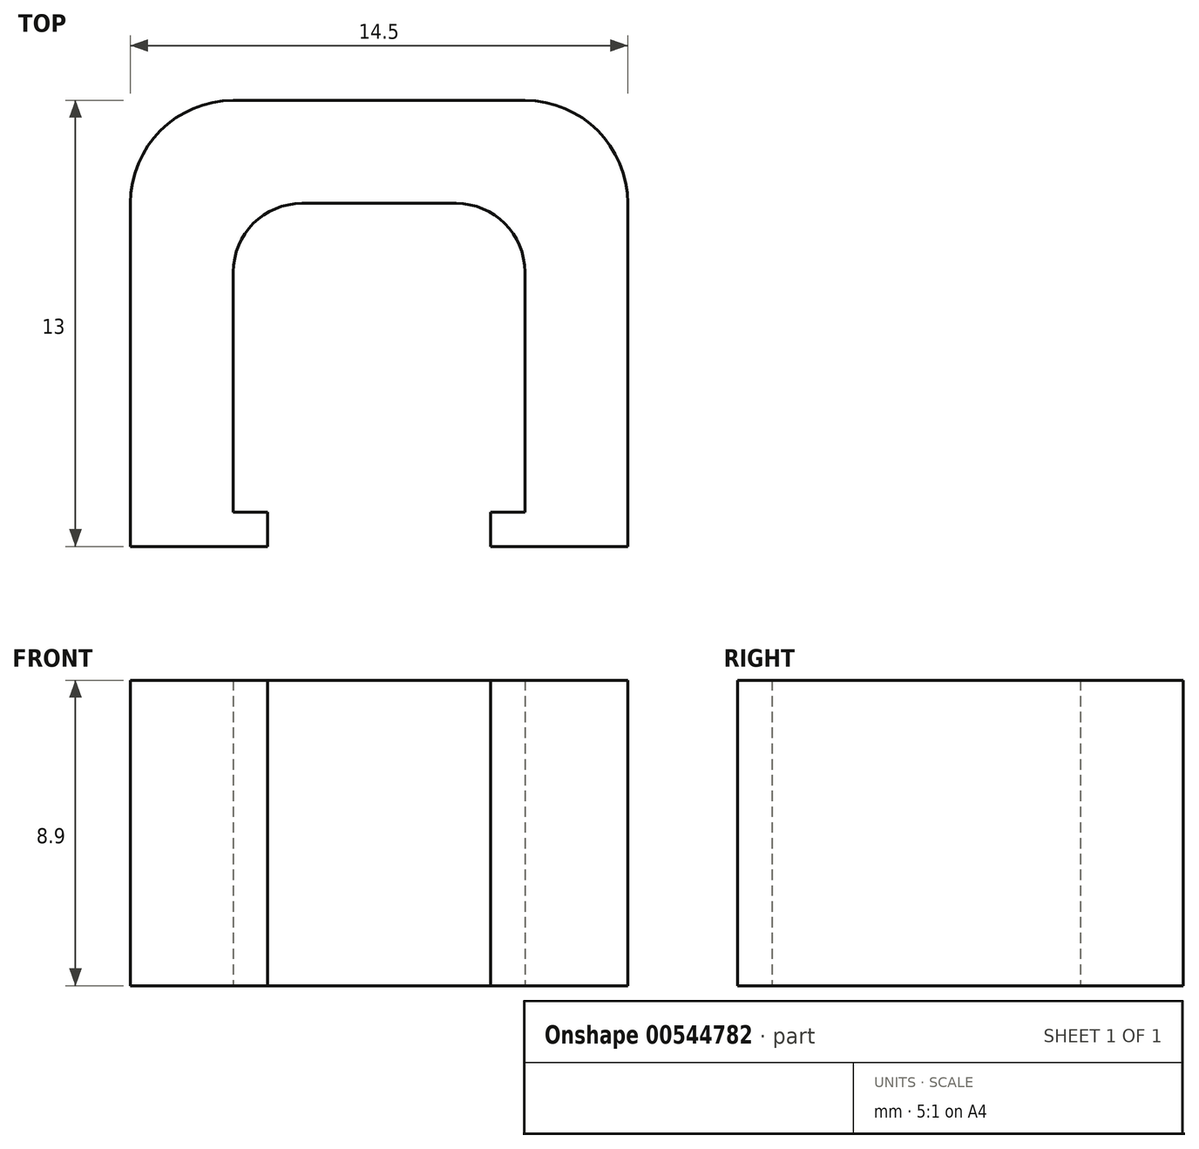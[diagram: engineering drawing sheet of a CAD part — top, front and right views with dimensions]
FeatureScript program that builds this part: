
annotation { "Feature Type Name" : "Feature", "Feature Type Description" : "" }
export const myFeature = defineFeature(function(context is Context, id is Id, definition is map)
    precondition{}
    {
        {
            var Q0;
            Q0=qCreatedBy(makeId("Top.planeOp"),FACE);
            var sketch = newSketch(context, id + "F0", { "sketchPlane" : qUnion([Q0])});
            skLineSegment(sketch, "E0", {"start": v(-14.5, 0) * mm, "end": v(-14.5, 10) * mm});
            skLineSegment(sketch, "E1", {"start": v(-11.5, 13) * mm, "end": v(-3, 13) * mm});
            skLineSegment(sketch, "E2", {"start": v(0, 10) * mm, "end": v(0, 0) * mm});
            skLineSegment(sketch, "E3.0", {"start": v(-3, 8) * mm, "end": v(-3, 0) * mm});
            skLineSegment(sketch, "E3.1", {"start": v(-9.5, 10) * mm, "end": v(-5, 10) * mm});
            skLineSegment(sketch, "E3.2", {"start": v(-11.5, 0) * mm, "end": v(-11.5, 8) * mm});
            skLineSegment(sketch, "E4", {"start": v(-3, 0) * mm, "end": v(-4, 0) * mm});
            skLineSegment(sketch, "E5", {"start": v(-4, 0) * mm, "end": v(-4, 1) * mm});
            skLineSegment(sketch, "E6", {"start": v(-4, 1) * mm, "end": v(-3, 1) * mm});
            skLineSegment(sketch, "E7", {"start": v(-3, 1) * mm, "end": v(-3, 0) * mm});
            skLineSegment(sketch, "E8", {"start": v(0, 0) * mm, "end": v(-3, 0) * mm});
            skLineSegment(sketch, "E9", {"start": v(-11.5, 0) * mm, "end": v(-14.5, 0) * mm});
            skLineSegment(sketch, "E10", {"start": v(-11.5, 1) * mm, "end": v(-10.5, 1) * mm});
            skLineSegment(sketch, "E11", {"start": v(-10.5, 1) * mm, "end": v(-10.5, 0) * mm});
            skLineSegment(sketch, "E12", {"start": v(-10.5, 0) * mm, "end": v(-11.5, 0) * mm});
            skPoint(sketch, "E13.visualSharp", {"position": v(-11.5, 10) * mm});
            skArc(sketch, "E13.filletArc", {"start": v(-9.5, 10) * mm, "mid": v(-10.91, 9.41) * mm, "end": v(-11.5, 8) * mm});
            skPoint(sketch, "E14.visualSharp", {"position": v(-3, 10) * mm});
            skArc(sketch, "E14.filletArc", {"start": v(-3, 8) * mm, "mid": v(-3.59, 9.41) * mm, "end": v(-5, 10) * mm});
            skPoint(sketch, "E15.visualSharp", {"position": v(0, 13) * mm});
            skArc(sketch, "E15.filletArc", {"start": v(0, 10) * mm, "mid": v(-0.88, 12.12) * mm, "end": v(-3, 13) * mm});
            skPoint(sketch, "E16.visualSharp", {"position": v(-14.5, 13) * mm});
            skArc(sketch, "E16.filletArc", {"start": v(-11.5, 13) * mm, "mid": v(-13.62, 12.12) * mm, "end": v(-14.5, 10) * mm});
            skSolve(sketch);
        }
        {
            var Q0;
            {var subQ2=sQuery(id+"F0.wireOp",EDGE,"E10");Q0=makeQuery(id+"F0.imprint","IMPRINT",FACE,{"disambiguationData":[TD([[makeQuery(id+"F0.imprint","IMPRINT",EDGE,{"derivedFrom":subQ2}),-1.0]])]});}
            var Q1;
            Q1=makeQuery(id+"F0.imprint","IMPRINT",FACE,{"disambiguationData":[TD([[makeQuery(id+"F0.imprint","IMPRINT",EDGE,{"derivedFrom":sQuery(id+"F0.wireOp",EDGE,"E0")}),-1.0]])]});
            var Q2;
            Q2=makeQuery(id+"F0.imprint","IMPRINT",FACE,{"disambiguationData":[TD([[makeQuery(id+"F0.imprint","IMPRINT",EDGE,{"derivedFrom":sQuery(id+"F0.wireOp",EDGE,"E4")}),-1.0]])]});
            extrude(context, id + "F1", {"entities" : qUnion([Q0, Q1, Q2]), "depth" : 8.9 * mm, "offsetDistance" : 25 * mm});
        }
    });
